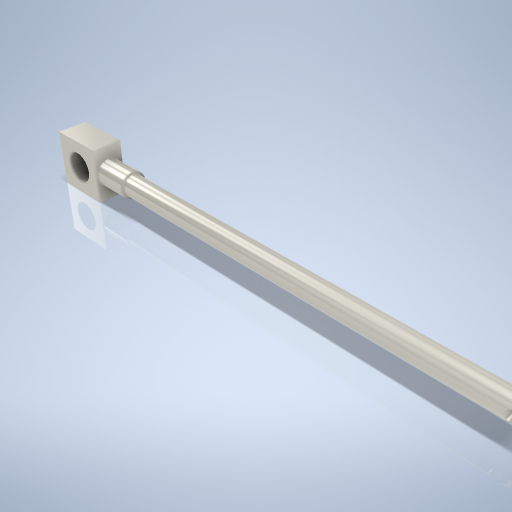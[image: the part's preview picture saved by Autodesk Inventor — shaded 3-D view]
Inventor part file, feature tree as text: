
AUTODESK INVENTOR PART (.ipt)
format: ipt  version: 2024.2 (Build 282272000, 272)  size: 293,888 bytes
history: native  units: mm
features: sketch x5, extrude x3, hole x2, plane x1, chamfer x1
ambient origin geometry x8: Origin, YZ Plane, XZ Plane, XY Plane, X Axis, Y Axis, Z Axis, Center Point
bodies: Volumenkörper1 (feature_tree)
feature tree (12):
  extrude  "Extrusion1"  Depth=10.0mm
  extrude  "Extrusion2"  Depth=5.0mm
  extrude  "Extrusion3"  Depth=4.0mm
  hole  "Bohrung1"  [1 undecoded]
  plane  "Arbeitsebene1"
  hole  "Bohrung2"  [1 undecoded]
  chamfer  "Fasen1"  Distance=1.0mm Angle=45.0deg
  sketch  "Skizze1"  dims[d0=10.0mm d1=10.0mm]
  sketch  "Skizze2"  dims[d2=5.5mm d3=0.0mm d4=5.0mm]
  sketch  "Skizze3"  dims[d5=6.5mm d6=0.0mm d7=4.0mm]
  sketch  "Skizze4"  dims[d8=74.0mm d9=0.0mm]
  sketch  "Skizze5"  dims[d10=5.5mm d11=6.0mm d12=4.0mm d13=2.0mm d14=90.0deg d15=3.0mm d16=0.0mm d17=2.0mm d18=2.5mm d19=2.0mm d20=6.0mm d21=4.0mm d22=2.0mm d23=90.0deg d24=8.0mm d25=0.0mm d26=1.0mm d27=2.0mm d28=45.0deg]
note: 2 required parameter values undecoded (feature->parameter linkage not recoverable at this tier; creation-order binding heuristic only, values carry confidence <= 0.55)
